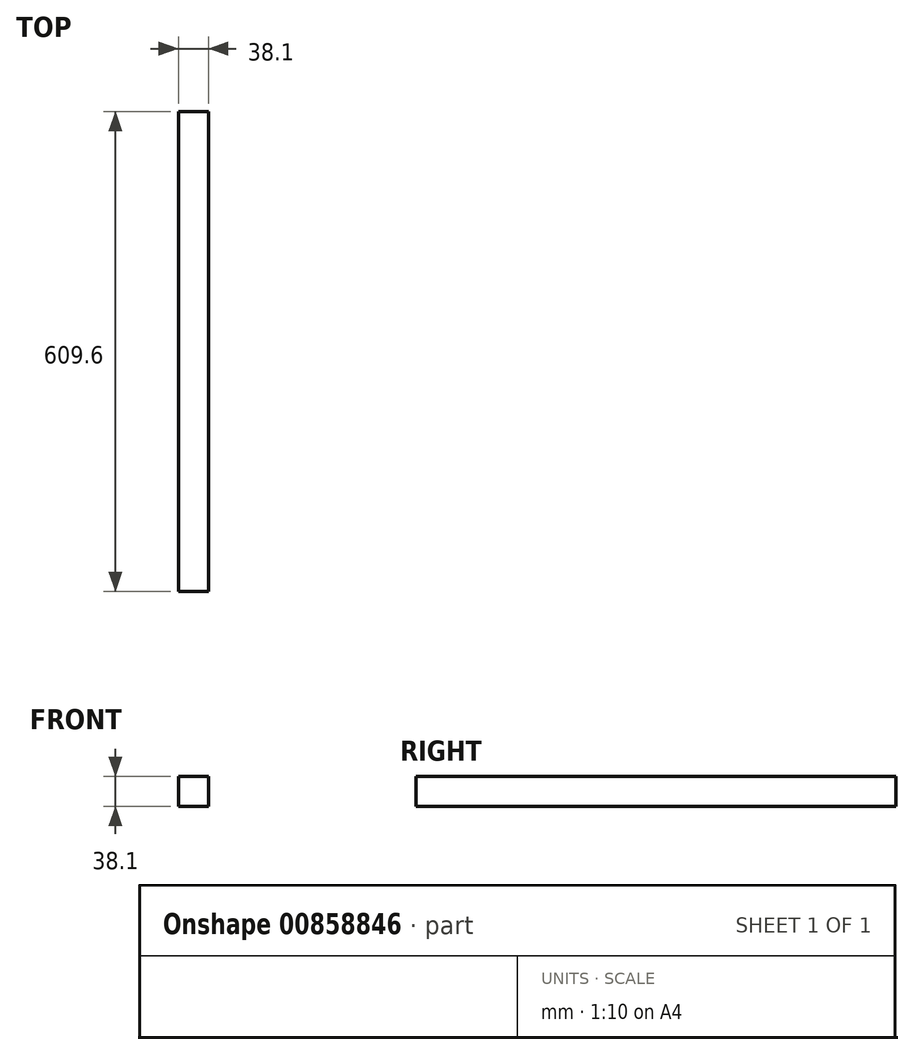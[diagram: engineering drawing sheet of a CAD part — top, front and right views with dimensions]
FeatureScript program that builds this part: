
annotation { "Feature Type Name" : "Feature", "Feature Type Description" : "" }
export const myFeature = defineFeature(function(context is Context, id is Id, definition is map)
    precondition{}
    {
        {
            var Q0;
            Q0=qCreatedBy(makeId("Front.planeOp"),FACE);
            var sketch = newSketch(context, id + "F0", { "sketchPlane" : qUnion([Q0])});
            skLineSegment(sketch, "E0.bottom", {"start": v(-75.86, 70.56) * mm, "end": v(-37.76, 70.56) * mm});
            skLineSegment(sketch, "E0.top", {"start": v(-75.86, 32.46) * mm, "end": v(-37.76, 32.46) * mm});
            skLineSegment(sketch, "E0.left", {"start": v(-75.86, 70.56) * mm, "end": v(-75.86, 32.46) * mm});
            skLineSegment(sketch, "E0.right", {"start": v(-37.76, 70.56) * mm, "end": v(-37.76, 32.46) * mm});
            skSolve(sketch);
        }
        {
            var Q0;
            Q0=makeQuery(id+"F0.imprint","IMPRINT",FACE,{"disambiguationData":[TD([[makeQuery(id+"F0.imprint","IMPRINT",EDGE,{"derivedFrom":sQuery(id+"F0.wireOp",EDGE,"E0.bottom")}),-1.0]])]});
            extrude(context, id + "F1", {"entities" : qUnion([Q0]), "depth" : 254 * mm, "offsetDistance" : 25.4 * mm});
        }
        {
            var Q0;
            Q0=makeQuery(id+"F1.opExtrude","CAP_FACE",FACE,{"disambiguationData":[OSD([sQuery(id+"F0.wireOp",EDGE,"E0.bottom"),sQuery(id+"F0.wireOp",EDGE,"E0.top"),sQuery(id+"F0.wireOp",EDGE,"E0.left"),sQuery(id+"F0.wireOp",EDGE,"E0.right")])],"isStart":true});
            extrude(context, id + "F2", {"entities" : qUnion([Q0]), "operationType" : NewBodyOperationType.ADD, "depth" : 101.6 * mm, "offsetDistance" : 25.4 * mm});
        }
        {
            var Q0;
            Q0=makeQuery(id+"F1.opExtrude","CAP_FACE",FACE,{"disambiguationData":[OSD([sQuery(id+"F0.wireOp",EDGE,"E0.bottom"),sQuery(id+"F0.wireOp",EDGE,"E0.top"),sQuery(id+"F0.wireOp",EDGE,"E0.left"),sQuery(id+"F0.wireOp",EDGE,"E0.right")])],"isStart":false});
            extrude(context, id + "F3", {"entities" : qUnion([Q0]), "operationType" : NewBodyOperationType.ADD, "depth" : 152.4 * mm, "offsetDistance" : 25.4 * mm});
        }
        {
            var Q0;
            Q0=makeQuery(id+"F3.opExtrude","CAP_FACE",FACE,{"disambiguationData":[OSD([sQuery(id+"F0.wireOp",EDGE,"E0.bottom"),sQuery(id+"F0.wireOp",EDGE,"E0.top"),sQuery(id+"F0.wireOp",EDGE,"E0.left"),sQuery(id+"F0.wireOp",EDGE,"E0.right")])],"isStart":false});
            extrude(context, id + "F4", {"entities" : qUnion([Q0]), "operationType" : NewBodyOperationType.ADD, "depth" : 101.6 * mm, "offsetDistance" : 25.4 * mm});
        }
    });
